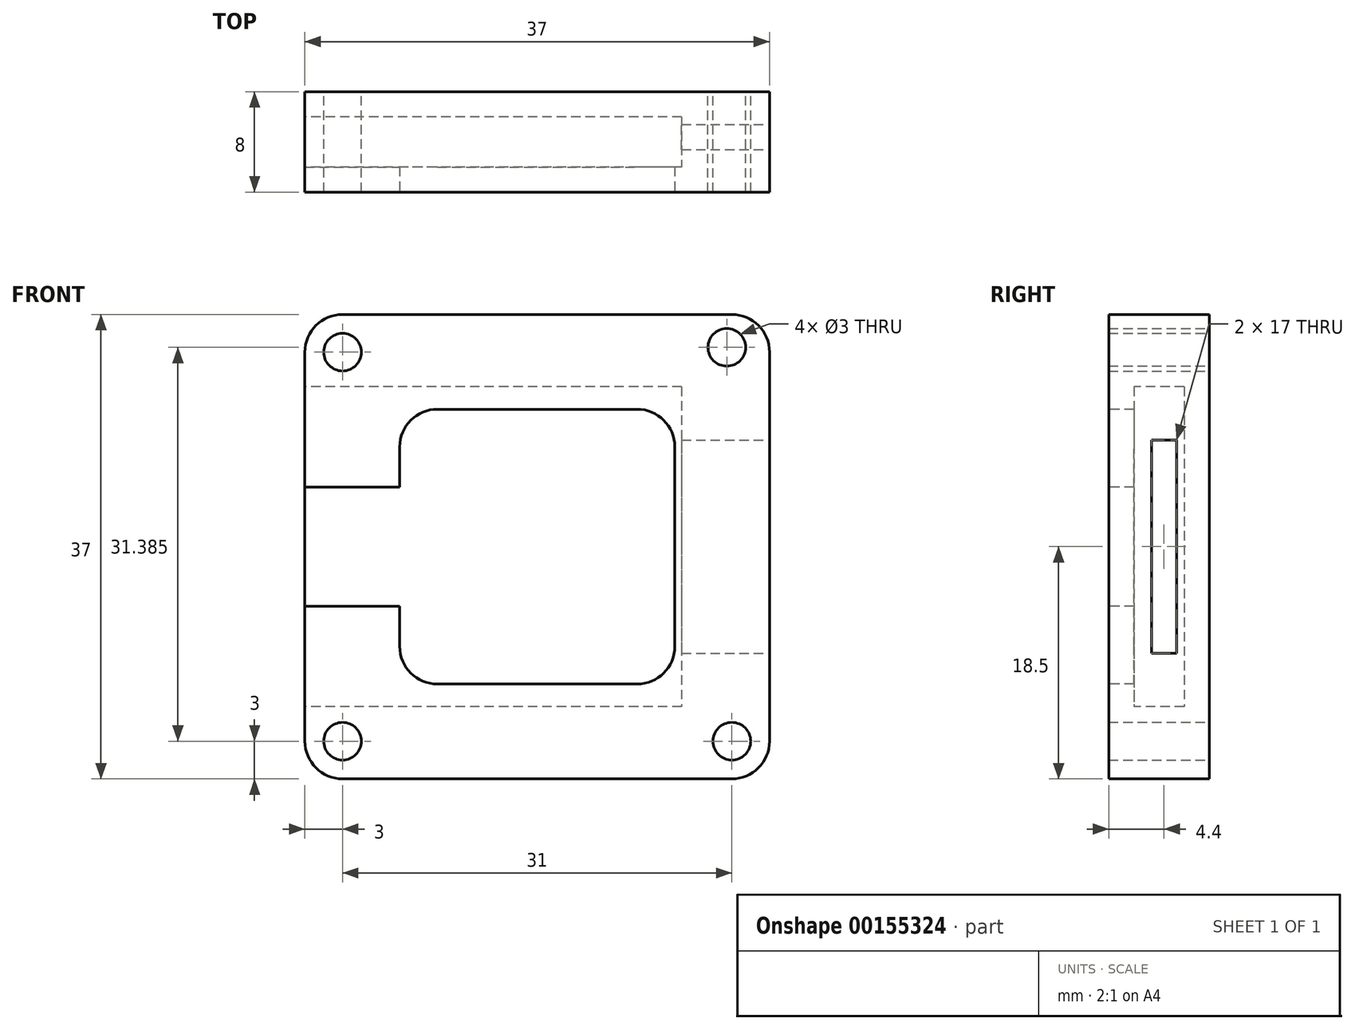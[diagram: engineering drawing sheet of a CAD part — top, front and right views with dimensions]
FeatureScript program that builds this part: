
annotation { "Feature Type Name" : "Feature", "Feature Type Description" : "" }
export const myFeature = defineFeature(function(context is Context, id is Id, definition is map)
    precondition{}
    {
        {
            var Q0;
            Q0=qCreatedBy(makeId("Front.planeOp"),FACE);
            var sketch = newSketch(context, id + "F0", { "sketchPlane" : qUnion([Q0])});
            skLineSegment(sketch, "E0.bottom", {"start": v(-15.5, 18.5) * mm, "end": v(15.5, 18.5) * mm});
            skLineSegment(sketch, "E0.top", {"start": v(-15.5, -18.5) * mm, "end": v(15.5, -18.5) * mm});
            skLineSegment(sketch, "E0.left", {"start": v(-18.5, 15.5) * mm, "end": v(-18.5, -15.5) * mm});
            skLineSegment(sketch, "E0.right", {"start": v(18.5, 15.5) * mm, "end": v(18.5, -15.5) * mm});
            skPoint(sketch, "E0.middle", {"position": v(0, 0) * mm});
            skPoint(sketch, "E1.visualSharp", {"position": v(18.5, 18.5) * mm});
            skArc(sketch, "E1.filletArc", {"start": v(18.5, 15.5) * mm, "mid": v(17.62, 17.62) * mm, "end": v(15.5, 18.5) * mm});
            skPoint(sketch, "E2.visualSharp", {"position": v(18.5, -18.5) * mm});
            skArc(sketch, "E2.filletArc", {"start": v(15.5, -18.5) * mm, "mid": v(17.62, -17.62) * mm, "end": v(18.5, -15.5) * mm});
            skPoint(sketch, "E3.visualSharp", {"position": v(-18.5, -18.5) * mm});
            skArc(sketch, "E3.filletArc", {"start": v(-18.5, -15.5) * mm, "mid": v(-17.62, -17.62) * mm, "end": v(-15.5, -18.5) * mm});
            skPoint(sketch, "E4.visualSharp", {"position": v(-18.5, 18.5) * mm});
            skArc(sketch, "E4.filletArc", {"start": v(-15.5, 18.5) * mm, "mid": v(-17.62, 17.62) * mm, "end": v(-18.5, 15.5) * mm});
            skCircle(sketch, "E5", {"center": v(-15.5, 15.5) * mm, "radius": 1.5 * mm});
            skCircle(sketch, "E6", {"center": v(15.1, 15.89) * mm, "radius": 1.5 * mm});
            skCircle(sketch, "E7", {"center": v(15.5, -15.5) * mm, "radius": 1.5 * mm});
            skCircle(sketch, "E8", {"center": v(-15.5, -15.5) * mm, "radius": 1.5 * mm});
            skSolve(sketch);
        }
        {
            var Q0;
            Q0=makeQuery(id+"F0.imprint","IMPRINT",FACE,{"disambiguationData":[TD([[makeQuery(id+"F0.imprint","IMPRINT",EDGE,{"derivedFrom":sQuery(id+"F0.wireOp",EDGE,"E0.bottom")}),-1.0]])]});
            extrude(context, id + "F1", {"entities" : qUnion([Q0]), "depth" : 8 * mm});
        }
        {
            var Q0;
            Q0=makeQuery(id+"F1.opExtrude","CAP_FACE",FACE,{"disambiguationData":[OSD([sQuery(id+"F0.wireOp",EDGE,"E0.bottom"),sQuery(id+"F0.wireOp",EDGE,"E0.top"),sQuery(id+"F0.wireOp",EDGE,"E0.left"),sQuery(id+"F0.wireOp",EDGE,"E0.right"),sQuery(id+"F0.wireOp",EDGE,"E1.filletArc"),sQuery(id+"F0.wireOp",EDGE,"E2.filletArc"),sQuery(id+"F0.wireOp",EDGE,"E3.filletArc"),sQuery(id+"F0.wireOp",EDGE,"E4.filletArc"),sQuery(id+"F0.wireOp",EDGE,"E5"),sQuery(id+"F0.wireOp",EDGE,"E6"),sQuery(id+"F0.wireOp",EDGE,"E7"),sQuery(id+"F0.wireOp",EDGE,"E8")])],"isStart":false});
            var sketch = newSketch(context, id + "F2", { "sketchPlane" : qUnion([Q0])});
            skLineSegment(sketch, "E9.bottom", {"start": v(-7.95, -10.95) * mm, "end": v(7.95, -10.95) * mm});
            skLineSegment(sketch, "E9.top", {"start": v(-7.95, 10.95) * mm, "end": v(7.95, 10.95) * mm});
            skLineSegment(sketch, "E9.left", {"start": v(-10.95, -7.95) * mm, "end": v(-10.95, 7.95) * mm});
            skLineSegment(sketch, "E9.right", {"start": v(10.95, -7.95) * mm, "end": v(10.95, 7.95) * mm});
            skPoint(sketch, "E9.middle", {"position": v(0, 0) * mm});
            skPoint(sketch, "E10.visualSharp", {"position": v(-10.95, -10.95) * mm});
            skArc(sketch, "E10.filletArc", {"start": v(-10.95, -7.95) * mm, "mid": v(-10.07, -10.07) * mm, "end": v(-7.95, -10.95) * mm});
            skPoint(sketch, "E11.visualSharp", {"position": v(-10.95, 10.95) * mm});
            skArc(sketch, "E11.filletArc", {"start": v(-7.95, 10.95) * mm, "mid": v(-10.07, 10.07) * mm, "end": v(-10.95, 7.95) * mm});
            skPoint(sketch, "E12.visualSharp", {"position": v(10.95, 10.95) * mm});
            skArc(sketch, "E12.filletArc", {"start": v(10.95, 7.95) * mm, "mid": v(10.07, 10.07) * mm, "end": v(7.95, 10.95) * mm});
            skPoint(sketch, "E13.visualSharp", {"position": v(10.95, -10.95) * mm});
            skArc(sketch, "E13.filletArc", {"start": v(7.95, -10.95) * mm, "mid": v(10.07, -10.07) * mm, "end": v(10.95, -7.95) * mm});
            skLineSegment(sketch, "E14.bottom", {"start": v(-18.5, -4.73) * mm, "end": v(-3.4, -4.73) * mm});
            skLineSegment(sketch, "E14.top", {"start": v(-18.5, 4.73) * mm, "end": v(-3.4, 4.73) * mm});
            skLineSegment(sketch, "E14.left", {"start": v(-18.5, -4.73) * mm, "end": v(-18.5, 4.73) * mm});
            skLineSegment(sketch, "E14.right", {"start": v(-3.4, -4.73) * mm, "end": v(-3.4, 4.73) * mm});
            skPoint(sketch, "E14.middle", {"position": v(-10.95, 0) * mm});
            skSolve(sketch);
        }
        {
            var Q0;
            Q0=qSketchRegion(id+"F2",true);
            extrude(context, id + "F3", {"entities" : qUnion([Q0]), "operationType" : NewBodyOperationType.REMOVE, "oppositeDirection" : true, "depth" : 6 * mm});
        }
        {
            var Q0;
            Q0=makeQuery(id+"F1.opExtrude","SWEPT_FACE",FACE,{"disambiguationData":[OSD([sQuery(id+"F0.wireOp",EDGE,"E0.right")])]});
            var sketch = newSketch(context, id + "F4", { "sketchPlane" : qUnion([Q0])});
            skLineSegment(sketch, "E15", {"start": v(0, 0) * mm, "end": v(-3.6, 0) * mm});
            skLineSegment(sketch, "E16.bottom", {"start": v(-4.6, 8.5) * mm, "end": v(-2.6, 8.5) * mm});
            skLineSegment(sketch, "E16.top", {"start": v(-4.6, -8.5) * mm, "end": v(-2.6, -8.5) * mm});
            skLineSegment(sketch, "E16.left", {"start": v(-4.6, 8.5) * mm, "end": v(-4.6, -8.5) * mm});
            skLineSegment(sketch, "E16.right", {"start": v(-2.6, 8.5) * mm, "end": v(-2.6, -8.5) * mm});
            skPoint(sketch, "E16.middle", {"position": v(-3.6, 0) * mm});
            skSolve(sketch);
        }
        {
            var Q0;
            {var subQ1=sQuery(id+"F4.wireOp",EDGE,"E16.bottom");Q0=makeQuery(id+"F4.imprint","IMPRINT",FACE,{"disambiguationData":[TD([[makeQuery(id+"F4.imprint","IMPRINT",EDGE,{"derivedFrom":subQ1}),-1.0]])]});}
            extrude(context, id + "F5", {"entities" : qUnion([Q0]), "operationType" : NewBodyOperationType.REMOVE, "oppositeDirection" : true, "depth" : 8 * mm});
        }
        {
            var Q0;
            Q0=makeQuery(id+"F1.opExtrude","SWEPT_FACE",FACE,{"disambiguationData":[OSD([sQuery(id+"F0.wireOp",EDGE,"E0.left")])]});
            var sketch = newSketch(context, id + "F6", { "sketchPlane" : qUnion([Q0])});
            skLineSegment(sketch, "E17", {"start": v(0, 0) * mm, "end": v(4, 0) * mm});
            skPoint(sketch, "E17.endSnap0", {"position": v(2, 0) * mm});
            skLineSegment(sketch, "E18.bottom", {"start": v(2, 12.75) * mm, "end": v(6, 12.75) * mm});
            skLineSegment(sketch, "E18.top", {"start": v(2, -12.75) * mm, "end": v(6, -12.75) * mm});
            skLineSegment(sketch, "E18.left", {"start": v(2, 12.75) * mm, "end": v(2, -12.75) * mm});
            skLineSegment(sketch, "E18.right", {"start": v(6, 12.75) * mm, "end": v(6, -12.75) * mm});
            skPoint(sketch, "E18.middle", {"position": v(4, 0) * mm});
            skSolve(sketch);
        }
        {
            var Q0;
            {var subQ0=sQuery(id+"F6.wireOp",EDGE,"E18.bottom");Q0=makeQuery(id+"F6.imprint","IMPRINT",FACE,{"disambiguationData":[TD([[makeQuery(id+"F6.imprint","IMPRINT",EDGE,{"derivedFrom":subQ0}),-1.0]])]});}
            var Q1;
            {var subQ0=sQuery(id+"F6.wireOp",EDGE,"E18.top");Q1=makeQuery(id+"F6.imprint","IMPRINT",FACE,{"disambiguationData":[TD([[makeQuery(id+"F6.imprint","IMPRINT",EDGE,{"derivedFrom":subQ0}),1.0]])]});}
            var Q2;
            {var subQ0=sQuery(id+"F6.wireOp",EDGE,"E18.left");var subQ9=makeQuery(id+"F6.imprint","INTERSECT",VERTEX,{"derivedFrom":[sQuery(id+"F6.wireOp",EDGE,"E17"),subQ0]});Q2=makeQuery(id+"F6.imprint","IMPRINT",FACE,{"disambiguationData":[TD([[makeQuery(id+"F6.imprint","IMPRINT",EDGE,{"disambiguationData":[TD([[subQ9,1.0]])],"derivedFrom":subQ0}),1.0]])]});}
            extrude(context, id + "F7", {"entities" : qUnion([Q0, Q1, Q2]), "operationType" : NewBodyOperationType.REMOVE, "oppositeDirection" : true, "depth" : 30 * mm});
        }
    });
